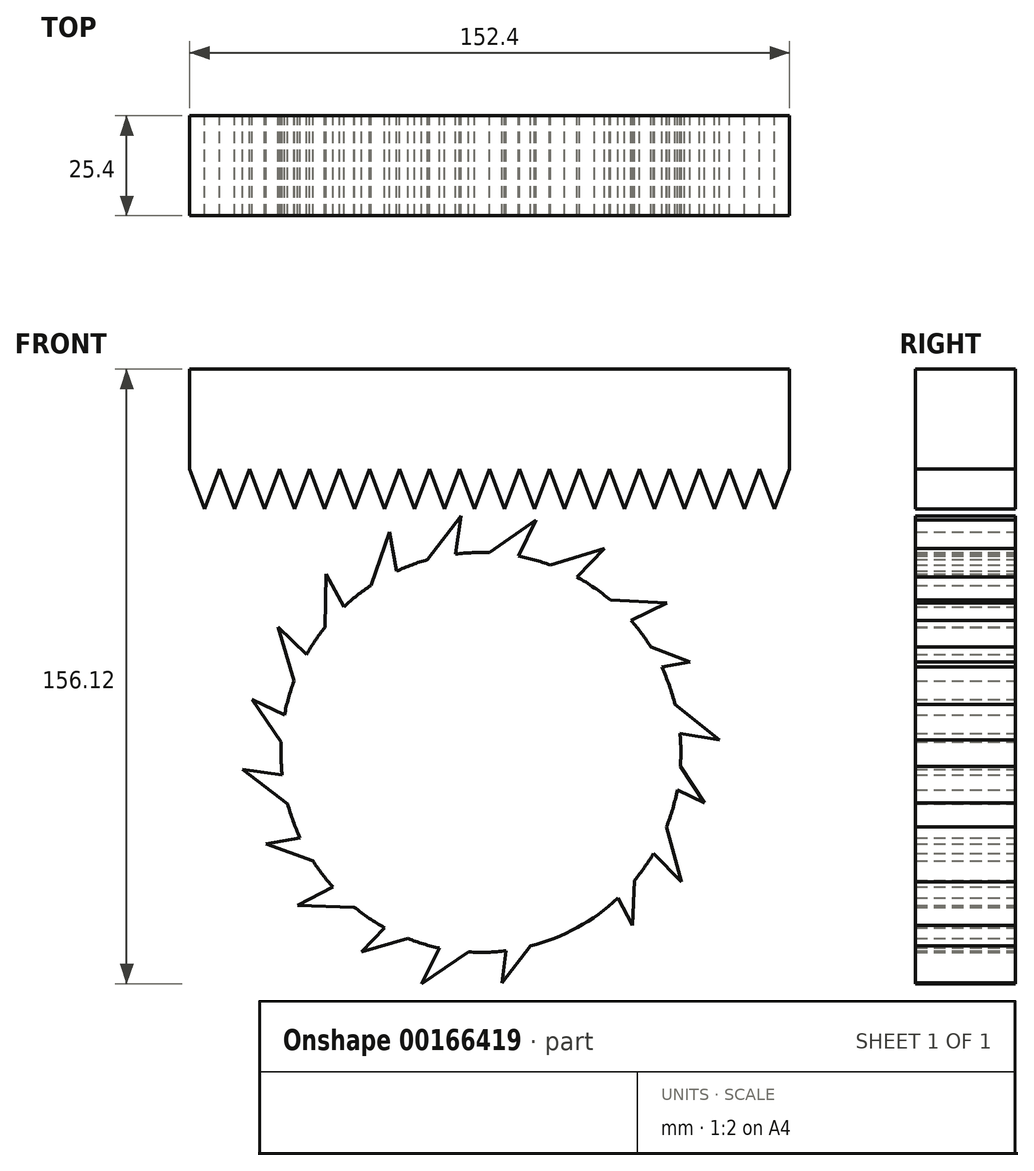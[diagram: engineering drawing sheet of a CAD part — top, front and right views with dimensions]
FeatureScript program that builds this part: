
annotation { "Feature Type Name" : "Feature", "Feature Type Description" : "" }
export const myFeature = defineFeature(function(context is Context, id is Id, definition is map)
    precondition{}
    {
        {
            var Q0;
            Q0=qCreatedBy(makeId("Front.planeOp"),FACE);
            var sketch = newSketch(context, id + "F0", { "sketchPlane" : qUnion([Q0])});
            skLineSegment(sketch, "E0.bottom", {"start": v(-77.76, 81.94) * mm, "end": v(74.64, 81.94) * mm});
            skLineSegment(sketch, "E0.top", {"start": v(-77.76, 56.54) * mm, "end": v(74.64, 56.54) * mm});
            skLineSegment(sketch, "E0.left", {"start": v(-77.76, 81.94) * mm, "end": v(-77.76, 56.54) * mm});
            skLineSegment(sketch, "E0.right", {"start": v(74.64, 81.94) * mm, "end": v(74.64, 56.54) * mm});
            skLineSegment(sketch, "E1", {"start": v(-77.76, 56.54) * mm, "end": v(-73.95, 46.38) * mm});
            skLineSegment(sketch, "E2", {"start": v(-73.95, 46.38) * mm, "end": v(-70.14, 56.54) * mm});
            skLineSegment(sketch, "E3.1.0.0", {"start": v(-70.14, 56.54) * mm, "end": v(-66.33, 46.38) * mm});
            skLineSegment(sketch, "E3.1.0.1", {"start": v(-66.33, 46.38) * mm, "end": v(-62.52, 56.54) * mm});
            skLineSegment(sketch, "E3.2.0.0", {"start": v(-62.52, 56.54) * mm, "end": v(-58.71, 46.38) * mm});
            skLineSegment(sketch, "E3.2.0.1", {"start": v(-58.71, 46.38) * mm, "end": v(-54.9, 56.54) * mm});
            skLineSegment(sketch, "E3.3.0.0", {"start": v(-54.9, 56.54) * mm, "end": v(-51.1, 46.38) * mm});
            skLineSegment(sketch, "E3.3.0.1", {"start": v(-51.1, 46.38) * mm, "end": v(-47.28, 56.54) * mm});
            skLineSegment(sketch, "E3.4.0.0", {"start": v(-47.28, 56.54) * mm, "end": v(-43.47, 46.38) * mm});
            skLineSegment(sketch, "E3.4.0.1", {"start": v(-43.47, 46.38) * mm, "end": v(-39.66, 56.54) * mm});
            skLineSegment(sketch, "E3.5.0.0", {"start": v(-39.66, 56.54) * mm, "end": v(-35.85, 46.38) * mm});
            skLineSegment(sketch, "E3.5.0.1", {"start": v(-35.85, 46.38) * mm, "end": v(-32.04, 56.54) * mm});
            skLineSegment(sketch, "E3.6.0.0", {"start": v(-32.04, 56.54) * mm, "end": v(-28.23, 46.38) * mm});
            skLineSegment(sketch, "E3.6.0.1", {"start": v(-28.23, 46.38) * mm, "end": v(-24.42, 56.54) * mm});
            skLineSegment(sketch, "E3.7.0.0", {"start": v(-24.42, 56.54) * mm, "end": v(-20.61, 46.38) * mm});
            skLineSegment(sketch, "E3.7.0.1", {"start": v(-20.61, 46.38) * mm, "end": v(-16.8, 56.54) * mm});
            skLineSegment(sketch, "E3.8.0.0", {"start": v(-16.8, 56.54) * mm, "end": v(-13, 46.38) * mm});
            skLineSegment(sketch, "E3.8.0.1", {"start": v(-13, 46.38) * mm, "end": v(-9.18, 56.54) * mm});
            skLineSegment(sketch, "E3.9.0.0", {"start": v(-9.18, 56.54) * mm, "end": v(-5.37, 46.38) * mm});
            skLineSegment(sketch, "E3.9.0.1", {"start": v(-5.37, 46.38) * mm, "end": v(-1.56, 56.54) * mm});
            skLineSegment(sketch, "E3.10.0.0", {"start": v(-1.56, 56.54) * mm, "end": v(2.25, 46.38) * mm});
            skLineSegment(sketch, "E3.10.0.1", {"start": v(2.25, 46.38) * mm, "end": v(6.06, 56.54) * mm});
            skLineSegment(sketch, "E3.11.0.0", {"start": v(6.06, 56.54) * mm, "end": v(9.87, 46.38) * mm});
            skLineSegment(sketch, "E3.11.0.1", {"start": v(9.87, 46.38) * mm, "end": v(13.68, 56.54) * mm});
            skLineSegment(sketch, "E3.12.0.0", {"start": v(13.68, 56.54) * mm, "end": v(17.49, 46.38) * mm});
            skLineSegment(sketch, "E3.12.0.1", {"start": v(17.49, 46.38) * mm, "end": v(21.3, 56.54) * mm});
            skLineSegment(sketch, "E3.13.0.0", {"start": v(21.3, 56.54) * mm, "end": v(25.1, 46.38) * mm});
            skLineSegment(sketch, "E3.13.0.1", {"start": v(25.1, 46.38) * mm, "end": v(28.92, 56.54) * mm});
            skLineSegment(sketch, "E3.14.0.0", {"start": v(28.92, 56.54) * mm, "end": v(32.73, 46.38) * mm});
            skLineSegment(sketch, "E3.14.0.1", {"start": v(32.73, 46.38) * mm, "end": v(36.54, 56.54) * mm});
            skLineSegment(sketch, "E3.15.0.0", {"start": v(36.54, 56.54) * mm, "end": v(40.35, 46.38) * mm});
            skLineSegment(sketch, "E3.15.0.1", {"start": v(40.35, 46.38) * mm, "end": v(44.16, 56.54) * mm});
            skLineSegment(sketch, "E3.16.0.0", {"start": v(44.16, 56.54) * mm, "end": v(47.97, 46.38) * mm});
            skLineSegment(sketch, "E3.16.0.1", {"start": v(47.97, 46.38) * mm, "end": v(51.78, 56.54) * mm});
            skLineSegment(sketch, "E3.17.0.0", {"start": v(51.78, 56.54) * mm, "end": v(55.59, 46.38) * mm});
            skLineSegment(sketch, "E3.17.0.1", {"start": v(55.59, 46.38) * mm, "end": v(59.4, 56.54) * mm});
            skLineSegment(sketch, "E3.18.0.0", {"start": v(59.4, 56.54) * mm, "end": v(63.2, 46.38) * mm});
            skLineSegment(sketch, "E3.18.0.1", {"start": v(63.2, 46.38) * mm, "end": v(67.02, 56.54) * mm});
            skLineSegment(sketch, "E3.19.0.0", {"start": v(67.02, 56.54) * mm, "end": v(70.83, 46.38) * mm});
            skLineSegment(sketch, "E3.19.0.1", {"start": v(70.83, 46.38) * mm, "end": v(74.64, 56.54) * mm});
            skLineSegment(sketch, "E3.direction1", {"start": v(-73.95, 46.38) * mm, "end": v(-66.33, 46.38) * mm, "construction": true});
            skSolve(sketch);
        }
        {
            var Q0;
            Q0=makeQuery(id+"F0.imprint","IMPRINT",FACE,{"disambiguationData":[TD([[makeQuery(id+"F0.imprint","IMPRINT",EDGE,{"derivedFrom":sQuery(id+"F0.wireOp",EDGE,"E0.bottom")}),-1.0]])]});
            var Q1;
            {var subQ0=sQuery(id+"F0.wireOp",EDGE,"E1");Q1=makeQuery(id+"F0.imprint","IMPRINT",FACE,{"disambiguationData":[TD([[makeQuery(id+"F0.imprint","IMPRINT",EDGE,{"derivedFrom":subQ0}),1.0]])]});}
            var Q2;
            {var subQ0=sQuery(id+"F0.wireOp",EDGE,"E3.1.0.0");Q2=makeQuery(id+"F0.imprint","IMPRINT",FACE,{"disambiguationData":[TD([[makeQuery(id+"F0.imprint","IMPRINT",EDGE,{"derivedFrom":subQ0}),1.0]])]});}
            var Q3;
            {var subQ0=sQuery(id+"F0.wireOp",EDGE,"E3.2.0.0");Q3=makeQuery(id+"F0.imprint","IMPRINT",FACE,{"disambiguationData":[TD([[makeQuery(id+"F0.imprint","IMPRINT",EDGE,{"derivedFrom":subQ0}),1.0]])]});}
            var Q4;
            {var subQ0=sQuery(id+"F0.wireOp",EDGE,"E3.3.0.0");Q4=makeQuery(id+"F0.imprint","IMPRINT",FACE,{"disambiguationData":[TD([[makeQuery(id+"F0.imprint","IMPRINT",EDGE,{"derivedFrom":subQ0}),1.0]])]});}
            var Q5;
            {var subQ0=sQuery(id+"F0.wireOp",EDGE,"E3.4.0.0");Q5=makeQuery(id+"F0.imprint","IMPRINT",FACE,{"disambiguationData":[TD([[makeQuery(id+"F0.imprint","IMPRINT",EDGE,{"derivedFrom":subQ0}),1.0]])]});}
            var Q6;
            {var subQ0=sQuery(id+"F0.wireOp",EDGE,"E3.5.0.0");Q6=makeQuery(id+"F0.imprint","IMPRINT",FACE,{"disambiguationData":[TD([[makeQuery(id+"F0.imprint","IMPRINT",EDGE,{"derivedFrom":subQ0}),1.0]])]});}
            var Q7;
            {var subQ0=sQuery(id+"F0.wireOp",EDGE,"E3.6.0.0");Q7=makeQuery(id+"F0.imprint","IMPRINT",FACE,{"disambiguationData":[TD([[makeQuery(id+"F0.imprint","IMPRINT",EDGE,{"derivedFrom":subQ0}),1.0]])]});}
            var Q8;
            {var subQ0=sQuery(id+"F0.wireOp",EDGE,"E3.7.0.0");Q8=makeQuery(id+"F0.imprint","IMPRINT",FACE,{"disambiguationData":[TD([[makeQuery(id+"F0.imprint","IMPRINT",EDGE,{"derivedFrom":subQ0}),1.0]])]});}
            var Q9;
            {var subQ0=sQuery(id+"F0.wireOp",EDGE,"E3.8.0.0");Q9=makeQuery(id+"F0.imprint","IMPRINT",FACE,{"disambiguationData":[TD([[makeQuery(id+"F0.imprint","IMPRINT",EDGE,{"derivedFrom":subQ0}),1.0]])]});}
            var Q10;
            {var subQ0=sQuery(id+"F0.wireOp",EDGE,"E3.9.0.0");Q10=makeQuery(id+"F0.imprint","IMPRINT",FACE,{"disambiguationData":[TD([[makeQuery(id+"F0.imprint","IMPRINT",EDGE,{"derivedFrom":subQ0}),1.0]])]});}
            var Q11;
            {var subQ0=sQuery(id+"F0.wireOp",EDGE,"E3.10.0.0");Q11=makeQuery(id+"F0.imprint","IMPRINT",FACE,{"disambiguationData":[TD([[makeQuery(id+"F0.imprint","IMPRINT",EDGE,{"derivedFrom":subQ0}),1.0]])]});}
            var Q12;
            {var subQ0=sQuery(id+"F0.wireOp",EDGE,"E3.11.0.0");Q12=makeQuery(id+"F0.imprint","IMPRINT",FACE,{"disambiguationData":[TD([[makeQuery(id+"F0.imprint","IMPRINT",EDGE,{"derivedFrom":subQ0}),1.0]])]});}
            var Q13;
            {var subQ0=sQuery(id+"F0.wireOp",EDGE,"E3.12.0.0");Q13=makeQuery(id+"F0.imprint","IMPRINT",FACE,{"disambiguationData":[TD([[makeQuery(id+"F0.imprint","IMPRINT",EDGE,{"derivedFrom":subQ0}),1.0]])]});}
            var Q14;
            {var subQ0=sQuery(id+"F0.wireOp",EDGE,"E3.13.0.0");Q14=makeQuery(id+"F0.imprint","IMPRINT",FACE,{"disambiguationData":[TD([[makeQuery(id+"F0.imprint","IMPRINT",EDGE,{"derivedFrom":subQ0}),1.0]])]});}
            var Q15;
            {var subQ0=sQuery(id+"F0.wireOp",EDGE,"E3.14.0.0");Q15=makeQuery(id+"F0.imprint","IMPRINT",FACE,{"disambiguationData":[TD([[makeQuery(id+"F0.imprint","IMPRINT",EDGE,{"derivedFrom":subQ0}),1.0]])]});}
            var Q16;
            {var subQ0=sQuery(id+"F0.wireOp",EDGE,"E3.15.0.0");Q16=makeQuery(id+"F0.imprint","IMPRINT",FACE,{"disambiguationData":[TD([[makeQuery(id+"F0.imprint","IMPRINT",EDGE,{"derivedFrom":subQ0}),1.0]])]});}
            var Q17;
            {var subQ0=sQuery(id+"F0.wireOp",EDGE,"E3.16.0.0");Q17=makeQuery(id+"F0.imprint","IMPRINT",FACE,{"disambiguationData":[TD([[makeQuery(id+"F0.imprint","IMPRINT",EDGE,{"derivedFrom":subQ0}),1.0]])]});}
            var Q18;
            {var subQ0=sQuery(id+"F0.wireOp",EDGE,"E3.17.0.0");Q18=makeQuery(id+"F0.imprint","IMPRINT",FACE,{"disambiguationData":[TD([[makeQuery(id+"F0.imprint","IMPRINT",EDGE,{"derivedFrom":subQ0}),1.0]])]});}
            var Q19;
            {var subQ0=sQuery(id+"F0.wireOp",EDGE,"E3.18.0.0");Q19=makeQuery(id+"F0.imprint","IMPRINT",FACE,{"disambiguationData":[TD([[makeQuery(id+"F0.imprint","IMPRINT",EDGE,{"derivedFrom":subQ0}),1.0]])]});}
            var Q20;
            {var subQ2=sQuery(id+"F0.wireOp",EDGE,"E3.19.0.0");Q20=makeQuery(id+"F0.imprint","IMPRINT",FACE,{"disambiguationData":[TD([[makeQuery(id+"F0.imprint","IMPRINT",EDGE,{"derivedFrom":subQ2}),1.0]])]});}
            extrude(context, id + "F1", {"entities" : qUnion([Q0, Q1, Q2, Q3, Q4, Q5, Q6, Q7, Q8, Q9, Q10, Q11, Q12, Q13, Q14, Q15, Q16, Q17, Q18, Q19, Q20]), "depth" : 25.4 * mm});
        }
        {
            var Q0;
            Q0=qCreatedBy(makeId("Front.planeOp"),FACE);
            var sketch = newSketch(context, id + "F2", { "sketchPlane" : qUnion([Q0])});
            skCircle(sketch, "E4", {"center": v(-3.8, -15.42) * mm, "radius": 50.8 * mm});
            skPoint(sketch, "E4.first.point", {"position": v(-54.52, -12.4) * mm});
            skPoint(sketch, "E4.second.point", {"position": v(-0.6, -66.12) * mm});
            skPoint(sketch, "E4.third.point", {"position": v(-40.68, -50.36) * mm});
            skLineSegment(sketch, "E5", {"start": v(-38.62, 21.58) * mm, "end": v(-43.43, 30.53) * mm});
            skLineSegment(sketch, "E6", {"start": v(-43.43, 30.53) * mm, "end": v(-43.65, 16.1) * mm});
            skLineSegment(sketch, "E7.1.0", {"start": v(-53.72, -5.95) * mm, "end": v(-62.87, -1.53) * mm});
            skLineSegment(sketch, "E7.1.1", {"start": v(-62.87, -1.53) * mm, "end": v(-54.57, -13.34) * mm});
            skLineSegment(sketch, "E7.2.0", {"start": v(-49.75, -37.1) * mm, "end": v(-59.75, -38.9) * mm});
            skLineSegment(sketch, "E7.2.1", {"start": v(-59.75, -38.9) * mm, "end": v(-46.1, -43.57) * mm});
            skLineSegment(sketch, "E7.3.0", {"start": v(-28.24, -59.96) * mm, "end": v(-35.26, -67.3) * mm});
            skLineSegment(sketch, "E7.3.1", {"start": v(-35.26, -67.3) * mm, "end": v(-21.47, -63.05) * mm});
            skLineSegment(sketch, "E7.4.0", {"start": v(2.6, -65.81) * mm, "end": v(1.24, -75.88) * mm});
            skLineSegment(sketch, "E7.4.1", {"start": v(1.24, -75.88) * mm, "end": v(9.9, -64.33) * mm});
            skLineSegment(sketch, "E7.5.0", {"start": v(31, -52.41) * mm, "end": v(35.81, -61.36) * mm});
            skLineSegment(sketch, "E7.5.1", {"start": v(35.81, -61.36) * mm, "end": v(36.03, -46.94) * mm});
            skLineSegment(sketch, "E7.6.0", {"start": v(46.1, -24.89) * mm, "end": v(55.25, -29.3) * mm});
            skLineSegment(sketch, "E7.6.1", {"start": v(55.25, -29.3) * mm, "end": v(46.95, -17.5) * mm});
            skLineSegment(sketch, "E7.7.0", {"start": v(42.13, 6.26) * mm, "end": v(52.13, 8.07) * mm});
            skLineSegment(sketch, "E7.7.1", {"start": v(52.13, 8.07) * mm, "end": v(38.48, 12.73) * mm});
            skLineSegment(sketch, "E7.8.0", {"start": v(20.62, 29.12) * mm, "end": v(27.65, 36.46) * mm});
            skLineSegment(sketch, "E7.8.1", {"start": v(27.65, 36.46) * mm, "end": v(13.86, 32.21) * mm});
            skLineSegment(sketch, "E7.9.0", {"start": v(-10.22, 34.98) * mm, "end": v(-8.86, 45.04) * mm});
            skLineSegment(sketch, "E7.9.1", {"start": v(-8.86, 45.04) * mm, "end": v(-17.51, 33.5) * mm});
            skLineSegment(sketch, "E8.1.0", {"start": v(10.18, 43.62) * mm, "end": v(-1.63, 35.34) * mm});
            skLineSegment(sketch, "E8.1.1", {"start": v(5.75, 34.47) * mm, "end": v(10.18, 43.62) * mm});
            skLineSegment(sketch, "E8.2.0", {"start": v(-8.63, 45.06) * mm, "end": v(-17.33, 33.55) * mm});
            skLineSegment(sketch, "E8.2.1", {"start": v(-10.04, 35) * mm, "end": v(-8.63, 45.06) * mm});
            skLineSegment(sketch, "E8.3.0", {"start": v(-26.98, 40.65) * mm, "end": v(-31.73, 27.02) * mm});
            skLineSegment(sketch, "E8.3.1", {"start": v(-25.23, 30.65) * mm, "end": v(-26.98, 40.65) * mm});
            skLineSegment(sketch, "E8.4.0", {"start": v(-43.1, 30.82) * mm, "end": v(-43.42, 16.4) * mm});
            skLineSegment(sketch, "E8.4.1", {"start": v(-38.35, 21.84) * mm, "end": v(-43.1, 30.82) * mm});
            skLineSegment(sketch, "E8.5.0", {"start": v(-55.4, 16.51) * mm, "end": v(-51.27, 2.68) * mm});
            skLineSegment(sketch, "E8.5.1", {"start": v(-48.12, 9.42) * mm, "end": v(-55.4, 16.51) * mm});
            skLineSegment(sketch, "E8.6.0", {"start": v(-62.71, -0.88) * mm, "end": v(-54.54, -12.78) * mm});
            skLineSegment(sketch, "E8.6.1", {"start": v(-53.61, -5.4) * mm, "end": v(-62.71, -0.88) * mm});
            skLineSegment(sketch, "E8.7.0", {"start": v(-64.33, -19.68) * mm, "end": v(-52.9, -28.5) * mm});
            skLineSegment(sketch, "E8.7.1", {"start": v(-54.28, -21.18) * mm, "end": v(-64.33, -19.68) * mm});
            skLineSegment(sketch, "E8.8.0", {"start": v(-60.1, -38.07) * mm, "end": v(-46.5, -42.94) * mm});
            skLineSegment(sketch, "E8.8.1", {"start": v(-50.07, -36.41) * mm, "end": v(-60.1, -38.07) * mm});
            skLineSegment(sketch, "E8.9.0", {"start": v(-50.4, -54.27) * mm, "end": v(-35.98, -54.73) * mm});
            skLineSegment(sketch, "E8.9.1", {"start": v(-41.38, -49.61) * mm, "end": v(-50.4, -54.27) * mm});
            skLineSegment(sketch, "E8.10.0", {"start": v(-36.21, -66.7) * mm, "end": v(-22.35, -62.71) * mm});
            skLineSegment(sketch, "E8.10.1", {"start": v(-29.05, -59.5) * mm, "end": v(-36.21, -66.7) * mm});
            skLineSegment(sketch, "E8.11.0", {"start": v(-18.88, -74.18) * mm, "end": v(-6.92, -66.12) * mm});
            skLineSegment(sketch, "E8.11.1", {"start": v(-14.29, -65.12) * mm, "end": v(-18.88, -74.18) * mm});
            skLineSegment(sketch, "E8.12.0", {"start": v(-0.1, -75.97) * mm, "end": v(8.81, -64.62) * mm});
            skLineSegment(sketch, "E8.12.1", {"start": v(1.5, -65.94) * mm, "end": v(-0.1, -75.97) * mm});
            skLineSegment(sketch, "E8.13.0", {"start": v(18.33, -71.9) * mm, "end": v(23.32, -58.36) * mm});
            skLineSegment(sketch, "E8.13.1", {"start": v(16.76, -61.87) * mm, "end": v(18.33, -71.9) * mm});
            skLineSegment(sketch, "E8.14.0", {"start": v(34.62, -62.37) * mm, "end": v(35.2, -47.95) * mm});
            skLineSegment(sketch, "E8.14.1", {"start": v(30.04, -53.3) * mm, "end": v(34.62, -62.37) * mm});
            skLineSegment(sketch, "E8.15.0", {"start": v(47.18, -48.3) * mm, "end": v(43.32, -34.39) * mm});
            skLineSegment(sketch, "E8.15.1", {"start": v(40.04, -41.06) * mm, "end": v(47.18, -48.3) * mm});
            skLineSegment(sketch, "E8.16.0", {"start": v(54.82, -31.03) * mm, "end": v(46.86, -18.99) * mm});
            skLineSegment(sketch, "E8.16.1", {"start": v(45.8, -26.35) * mm, "end": v(54.82, -31.03) * mm});
            skLineSegment(sketch, "E8.17.0", {"start": v(56.78, -12.26) * mm, "end": v(45.51, -3.25) * mm});
            skLineSegment(sketch, "E8.17.1", {"start": v(46.76, -10.58) * mm, "end": v(56.78, -12.26) * mm});
            skLineSegment(sketch, "E8.18.0", {"start": v(52.88, 6.2) * mm, "end": v(39.39, 11.32) * mm});
            skLineSegment(sketch, "E8.18.1", {"start": v(42.83, 4.73) * mm, "end": v(52.88, 6.2) * mm});
            skLineSegment(sketch, "E8.19.0", {"start": v(43.5, 22.58) * mm, "end": v(29.08, 23.3) * mm});
            skLineSegment(sketch, "E8.19.1", {"start": v(34.38, 18.08) * mm, "end": v(43.5, 22.58) * mm});
            skLineSegment(sketch, "E8.anchor1", {"start": v(-3.8, -15.42) * mm, "end": v(20.62, 29.12) * mm, "construction": true});
            skLineSegment(sketch, "E8.anchor2", {"start": v(-3.8, -15.42) * mm, "end": v(34.38, 18.08) * mm, "construction": true});
            skSolve(sketch);
        }
        {
            var Q0;
            {var subQ0=sQuery(id+"F2.wireOp",EDGE,"E4");var subQ46=makeQuery(id+"F2.imprint","INTERSECT",VERTEX,{"derivedFrom":[subQ0,sQuery(id+"F2.wireOp",EDGE,"E8.17.0")]});Q0=makeQuery(id+"F2.imprint","IMPRINT",FACE,{"disambiguationData":[TD([[makeQuery(id+"F2.imprint","IMPRINT",EDGE,{"disambiguationData":[TD([[subQ46,1.0]])],"derivedFrom":subQ0}),1.0]])]});}
            var Q1;
            {var subQ0=sQuery(id+"F2.wireOp",EDGE,"E8.5.0");Q1=makeQuery(id+"F2.imprint","IMPRINT",FACE,{"disambiguationData":[TD([[makeQuery(id+"F2.imprint","IMPRINT",EDGE,{"derivedFrom":subQ0}),1.0]])]});}
            var Q2;
            {var subQ0=sQuery(id+"F2.wireOp",EDGE,"E5");var subQ1=sQuery(id+"F2.wireOp",EDGE,"E4");var subQ2=makeQuery(id+"F2.imprint","INTERSECT",VERTEX,{"derivedFrom":[subQ1,subQ0]});Q2=makeQuery(id+"F2.imprint","IMPRINT",FACE,{"disambiguationData":[TD([[makeQuery(id+"F2.imprint","IMPRINT",EDGE,{"disambiguationData":[TD([[subQ2,-1.0]])],"derivedFrom":subQ1}),-1.0]])]});}
            var Q3;
            {var subQ0=sQuery(id+"F2.wireOp",EDGE,"E8.3.0");Q3=makeQuery(id+"F2.imprint","IMPRINT",FACE,{"disambiguationData":[TD([[makeQuery(id+"F2.imprint","IMPRINT",EDGE,{"derivedFrom":subQ0}),1.0]])]});}
            var Q4;
            {var subQ0=sQuery(id+"F2.wireOp",EDGE,"E7.9.0");var subQ1=sQuery(id+"F2.wireOp",EDGE,"E4");var subQ2=makeQuery(id+"F2.imprint","INTERSECT",VERTEX,{"derivedFrom":[subQ1,subQ0]});Q4=makeQuery(id+"F2.imprint","IMPRINT",FACE,{"disambiguationData":[TD([[makeQuery(id+"F2.imprint","IMPRINT",EDGE,{"disambiguationData":[TD([[subQ2,-1.0]])],"derivedFrom":subQ1}),-1.0]])]});}
            var Q5;
            {var subQ0=sQuery(id+"F2.wireOp",EDGE,"E8.1.0");Q5=makeQuery(id+"F2.imprint","IMPRINT",FACE,{"disambiguationData":[TD([[makeQuery(id+"F2.imprint","IMPRINT",EDGE,{"derivedFrom":subQ0}),1.0]])]});}
            var Q6;
            {var subQ0=sQuery(id+"F2.wireOp",EDGE,"E7.8.0");Q6=makeQuery(id+"F2.imprint","IMPRINT",FACE,{"disambiguationData":[TD([[makeQuery(id+"F2.imprint","IMPRINT",EDGE,{"derivedFrom":subQ0}),1.0]])]});}
            var Q7;
            {var subQ0=sQuery(id+"F2.wireOp",EDGE,"E8.19.0");Q7=makeQuery(id+"F2.imprint","IMPRINT",FACE,{"disambiguationData":[TD([[makeQuery(id+"F2.imprint","IMPRINT",EDGE,{"derivedFrom":subQ0}),1.0]])]});}
            var Q8;
            {var subQ0=sQuery(id+"F2.wireOp",EDGE,"E7.7.0");var subQ1=sQuery(id+"F2.wireOp",EDGE,"E4");var subQ2=makeQuery(id+"F2.imprint","INTERSECT",VERTEX,{"derivedFrom":[subQ1,subQ0]});Q8=makeQuery(id+"F2.imprint","IMPRINT",FACE,{"disambiguationData":[TD([[makeQuery(id+"F2.imprint","IMPRINT",EDGE,{"disambiguationData":[TD([[subQ2,-1.0]])],"derivedFrom":subQ1}),-1.0]])]});}
            var Q9;
            {var subQ0=sQuery(id+"F2.wireOp",EDGE,"E8.17.0");Q9=makeQuery(id+"F2.imprint","IMPRINT",FACE,{"disambiguationData":[TD([[makeQuery(id+"F2.imprint","IMPRINT",EDGE,{"derivedFrom":subQ0}),1.0]])]});}
            var Q10;
            {var subQ0=sQuery(id+"F2.wireOp",EDGE,"E7.6.0");var subQ1=sQuery(id+"F2.wireOp",EDGE,"E4");var subQ2=makeQuery(id+"F2.imprint","INTERSECT",VERTEX,{"derivedFrom":[subQ1,subQ0]});Q10=makeQuery(id+"F2.imprint","IMPRINT",FACE,{"disambiguationData":[TD([[makeQuery(id+"F2.imprint","IMPRINT",EDGE,{"disambiguationData":[TD([[subQ2,-1.0]])],"derivedFrom":subQ1}),-1.0]])]});}
            var Q11;
            {var subQ0=sQuery(id+"F2.wireOp",EDGE,"E8.15.0");Q11=makeQuery(id+"F2.imprint","IMPRINT",FACE,{"disambiguationData":[TD([[makeQuery(id+"F2.imprint","IMPRINT",EDGE,{"derivedFrom":subQ0}),1.0]])]});}
            var Q12;
            {var subQ0=sQuery(id+"F2.wireOp",EDGE,"E7.5.0");var subQ1=sQuery(id+"F2.wireOp",EDGE,"E4");var subQ2=makeQuery(id+"F2.imprint","INTERSECT",VERTEX,{"derivedFrom":[subQ1,subQ0]});Q12=makeQuery(id+"F2.imprint","IMPRINT",FACE,{"disambiguationData":[TD([[makeQuery(id+"F2.imprint","IMPRINT",EDGE,{"disambiguationData":[TD([[subQ2,-1.0]])],"derivedFrom":subQ1}),-1.0]])]});}
            var Q13;
            {var subQ0=sQuery(id+"F2.wireOp",EDGE,"E7.4.0");var subQ1=sQuery(id+"F2.wireOp",EDGE,"E4");var subQ2=makeQuery(id+"F2.imprint","INTERSECT",VERTEX,{"derivedFrom":[subQ1,subQ0]});Q13=makeQuery(id+"F2.imprint","IMPRINT",FACE,{"disambiguationData":[TD([[makeQuery(id+"F2.imprint","IMPRINT",EDGE,{"disambiguationData":[TD([[subQ2,-1.0]])],"derivedFrom":subQ1}),-1.0]])]});}
            var Q14;
            {var subQ0=sQuery(id+"F2.wireOp",EDGE,"E8.11.0");Q14=makeQuery(id+"F2.imprint","IMPRINT",FACE,{"disambiguationData":[TD([[makeQuery(id+"F2.imprint","IMPRINT",EDGE,{"derivedFrom":subQ0}),1.0]])]});}
            var Q15;
            {var subQ0=sQuery(id+"F2.wireOp",EDGE,"E7.3.0");var subQ1=sQuery(id+"F2.wireOp",EDGE,"E4");var subQ2=makeQuery(id+"F2.imprint","INTERSECT",VERTEX,{"derivedFrom":[subQ1,subQ0]});Q15=makeQuery(id+"F2.imprint","IMPRINT",FACE,{"disambiguationData":[TD([[makeQuery(id+"F2.imprint","IMPRINT",EDGE,{"disambiguationData":[TD([[subQ2,-1.0]])],"derivedFrom":subQ1}),-1.0]])]});}
            var Q16;
            {var subQ0=sQuery(id+"F2.wireOp",EDGE,"E8.9.0");Q16=makeQuery(id+"F2.imprint","IMPRINT",FACE,{"disambiguationData":[TD([[makeQuery(id+"F2.imprint","IMPRINT",EDGE,{"derivedFrom":subQ0}),1.0]])]});}
            var Q17;
            {var subQ0=sQuery(id+"F2.wireOp",EDGE,"E7.2.0");var subQ1=sQuery(id+"F2.wireOp",EDGE,"E4");var subQ2=makeQuery(id+"F2.imprint","INTERSECT",VERTEX,{"derivedFrom":[subQ1,subQ0]});Q17=makeQuery(id+"F2.imprint","IMPRINT",FACE,{"disambiguationData":[TD([[makeQuery(id+"F2.imprint","IMPRINT",EDGE,{"disambiguationData":[TD([[subQ2,-1.0]])],"derivedFrom":subQ1}),-1.0]])]});}
            var Q18;
            {var subQ0=sQuery(id+"F2.wireOp",EDGE,"E8.7.0");Q18=makeQuery(id+"F2.imprint","IMPRINT",FACE,{"disambiguationData":[TD([[makeQuery(id+"F2.imprint","IMPRINT",EDGE,{"derivedFrom":subQ0}),1.0]])]});}
            var Q19;
            {var subQ0=sQuery(id+"F2.wireOp",EDGE,"E7.1.0");var subQ1=sQuery(id+"F2.wireOp",EDGE,"E4");var subQ2=makeQuery(id+"F2.imprint","INTERSECT",VERTEX,{"derivedFrom":[subQ1,subQ0]});Q19=makeQuery(id+"F2.imprint","IMPRINT",FACE,{"disambiguationData":[TD([[makeQuery(id+"F2.imprint","IMPRINT",EDGE,{"disambiguationData":[TD([[subQ2,-1.0]])],"derivedFrom":subQ1}),-1.0]])]});}
            extrude(context, id + "F3", {"entities" : qUnion([Q0, Q1, Q2, Q3, Q4, Q5, Q6, Q7, Q8, Q9, Q10, Q11, Q12, Q13, Q14, Q15, Q16, Q17, Q18, Q19]), "depth" : 25.4 * mm});
        }
    });
